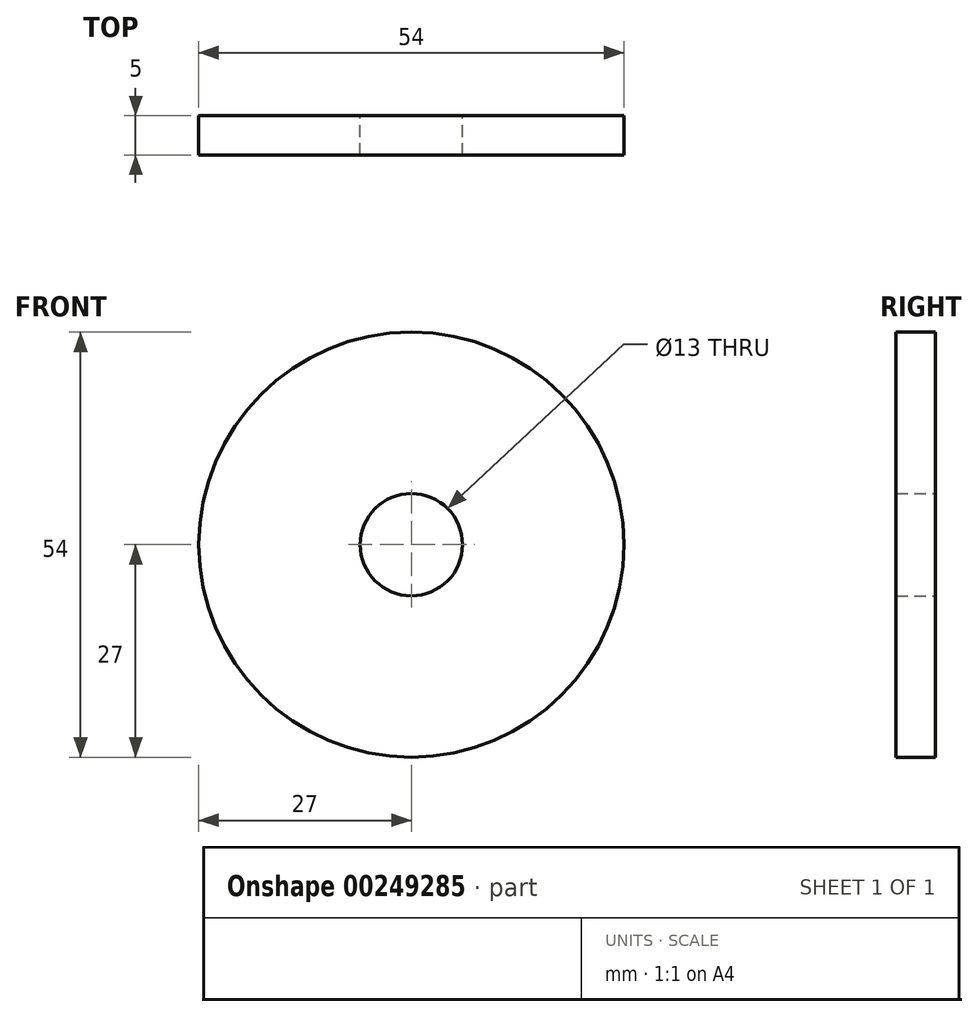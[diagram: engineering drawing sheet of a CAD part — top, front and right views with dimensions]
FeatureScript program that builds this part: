
annotation { "Feature Type Name" : "Feature", "Feature Type Description" : "" }
export const myFeature = defineFeature(function(context is Context, id is Id, definition is map)
    precondition{}
    {
        {
            var Q0;
            Q0=qCreatedBy(makeId("Front.planeOp"),FACE);
            var sketch = newSketch(context, id + "F0", { "sketchPlane" : qUnion([Q0])});
            skCircle(sketch, "E0", {"center": v(0, 0) * mm, "radius": 6.5 * mm});
            skCircle(sketch, "E1", {"center": v(0, 0) * mm, "radius": 27 * mm});
            skSolve(sketch);
        }
        {
            var Q0;
            Q0=makeQuery(id+"F0.imprint","IMPRINT",FACE,{"disambiguationData":[TD([[makeQuery(id+"F0.imprint","IMPRINT",EDGE,{"derivedFrom":sQuery(id+"F0.wireOp",EDGE,"E0")}),-1.0]])]});
            extrude(context, id + "F1", {"entities" : qUnion([Q0]), "depth" : 5 * mm, "offsetDistance" : 25 * mm, "symmetric" : true});
        }
    });
